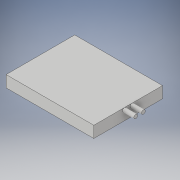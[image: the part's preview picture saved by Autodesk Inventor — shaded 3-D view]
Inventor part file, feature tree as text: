
AUTODESK INVENTOR PART (.ipt)
format: ipt  version: 2017 (Build 210142000, 142)  size: 102,912 bytes
history: native  units: in
note: dims shown in document units (in); Inventor stores cm internally (conversion verified against a paired STEP export)
features: extrude x2, sketch x2
ambient origin geometry x8: Origin, YZ Plane, XZ Plane, XY Plane, X Axis, Y Axis, Z Axis, Center Point
bodies: Solid1 (feature_tree)
feature tree (4):
  extrude  "Extrusion1"  Depth=1.125in
  extrude  "Extrusion2"  Depth=0.1875in
  sketch  "Sketch1"  dims[d0=1.4375in d1=1.125in]
  sketch  "Sketch3"  dims[d2=0.1875in d3=0.0in d5=0.5in d7=0.5in d8=0.1875in d9=0.0in d10=0.0625in d11=0.0625in]
